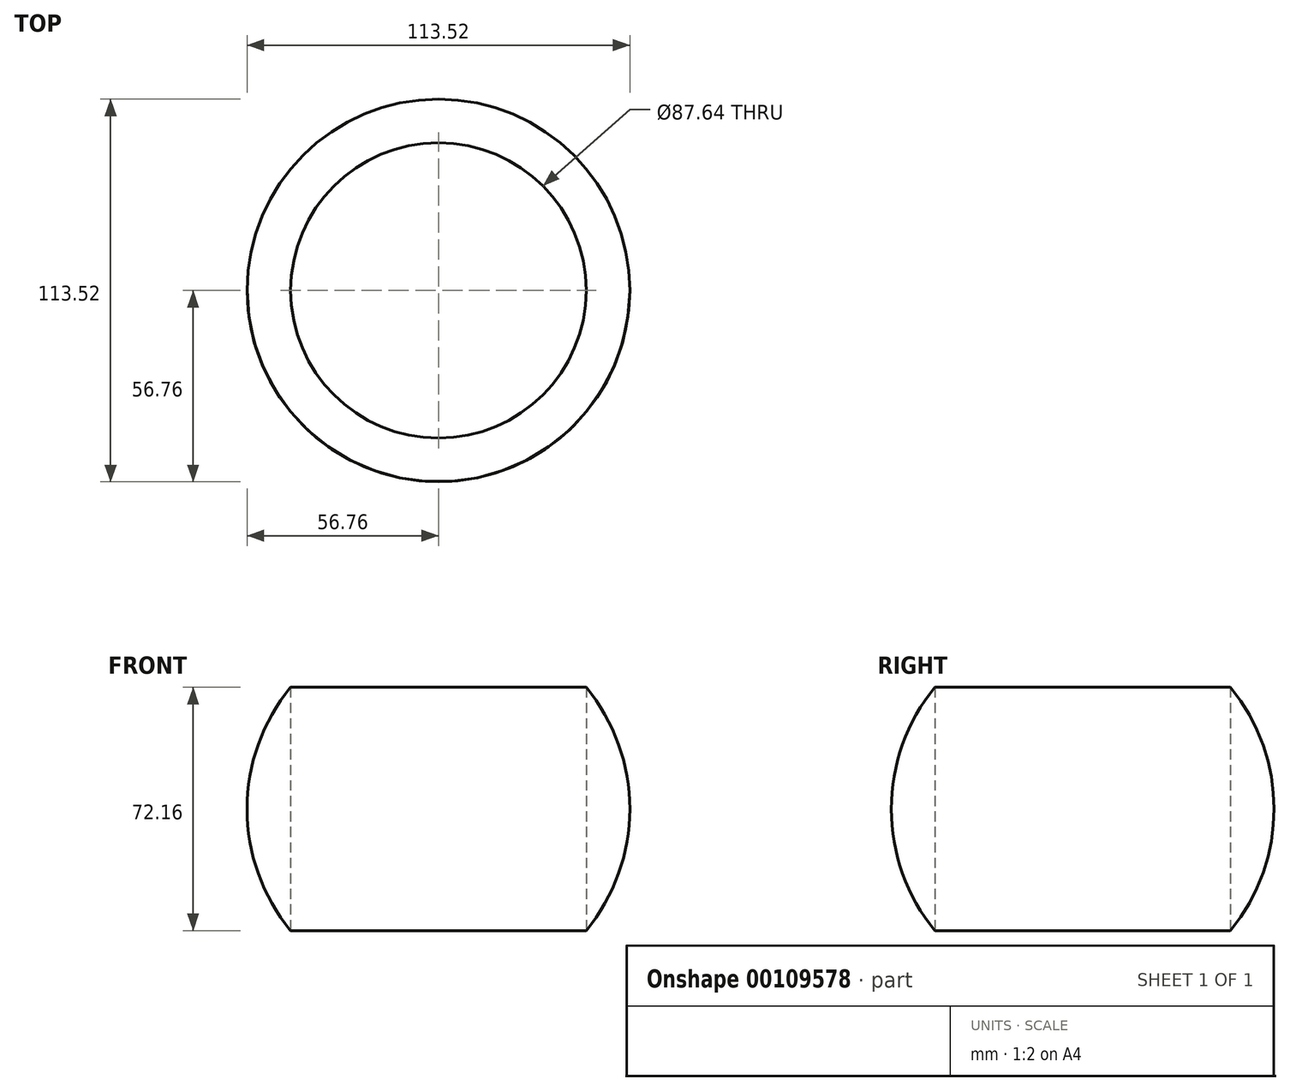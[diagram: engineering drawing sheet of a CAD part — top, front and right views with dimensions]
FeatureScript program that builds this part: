
annotation { "Feature Type Name" : "Feature", "Feature Type Description" : "" }
export const myFeature = defineFeature(function(context is Context, id is Id, definition is map)
    precondition{}
    {
        {
            var Q0;
            Q0=qCreatedBy(makeId("Front.planeOp"),FACE);
            var sketch = newSketch(context, id + "F0", { "sketchPlane" : qUnion([Q0])});
            skLineSegment(sketch, "E0", {"start": v(-76.44, 0) * mm, "end": v(75.59, 0) * mm});
            skArc(sketch, "E1", {"start": v(56.76, 0) * mm, "mid": v(0, 56.76) * mm, "end": v(-56.76, 0) * mm});
            skSolve(sketch);
        }
        {
            var Q0;
            {var subQ0=sQuery(id+"F0.wireOp",EDGE,"E1");Q0=makeQuery(id+"F0.imprint","IMPRINT",FACE,{"disambiguationData":[TD([[makeQuery(id+"F0.imprint","IMPRINT",EDGE,{"derivedFrom":subQ0}),1.0]])]});}
            var Q1;
            Q1=sQuery(id+"F0.wireOp",EDGE,"E0");
            revolve(context, id + "F1", {"entities" : qUnion([Q0]), "axis" : qUnion([Q1]), "revolveType" : RevolveType.FULL});
        }
        {
            var Q0;
            Q0=qCreatedBy(makeId("Front.planeOp"),FACE);
            var sketch = newSketch(context, id + "F2", { "sketchPlane" : qUnion([Q0])});
            skLineSegment(sketch, "E2.bottom", {"start": v(-60.76, 64.9) * mm, "end": v(57.62, 64.9) * mm});
            skLineSegment(sketch, "E2.top", {"start": v(-60.76, 36.08) * mm, "end": v(57.62, 36.08) * mm});
            skLineSegment(sketch, "E2.left", {"start": v(-60.76, 64.9) * mm, "end": v(-60.76, 36.08) * mm});
            skLineSegment(sketch, "E2.right", {"start": v(57.62, 64.9) * mm, "end": v(57.62, 36.08) * mm});
            skLineSegment(sketch, "E3.bottom", {"start": v(-66.18, -36.08) * mm, "end": v(59.33, -36.08) * mm});
            skLineSegment(sketch, "E3.top", {"start": v(-66.18, -63.47) * mm, "end": v(59.33, -63.47) * mm});
            skLineSegment(sketch, "E3.left", {"start": v(-66.18, -36.08) * mm, "end": v(-66.18, -63.47) * mm});
            skLineSegment(sketch, "E3.right", {"start": v(59.33, -36.08) * mm, "end": v(59.33, -63.47) * mm});
            skSolve(sketch);
        }
        {
            var Q0;
            Q0 = qSketchRegion(id + "F2", true);
            extrude(context, id + "F3", {"entities" : qUnion([Q0]), "operationType" : NewBodyOperationType.REMOVE, "depth" : 52.58 * mm, "hasSecondDirection" : true, "secondDirectionOppositeDirection" : true, "secondDirectionDepth" : 60.15 * mm});
        }
        {
            var Q0;
            Q0=makeQuery(id+"F3.boolean.opBoolean","COPY",FACE,{"derivedFrom":makeQuery(id+"F3.opExtrude","SWEPT_FACE",FACE,{"disambiguationData":[OSD([sQuery(id+"F2.wireOp",EDGE,"E3.bottom")])]})});
            extrude(context, id + "F4", {"entities" : qUnion([Q0]), "operationType" : NewBodyOperationType.REMOVE, "oppositeDirection" : true, "depth" : 107.12 * mm});
        }
    });
